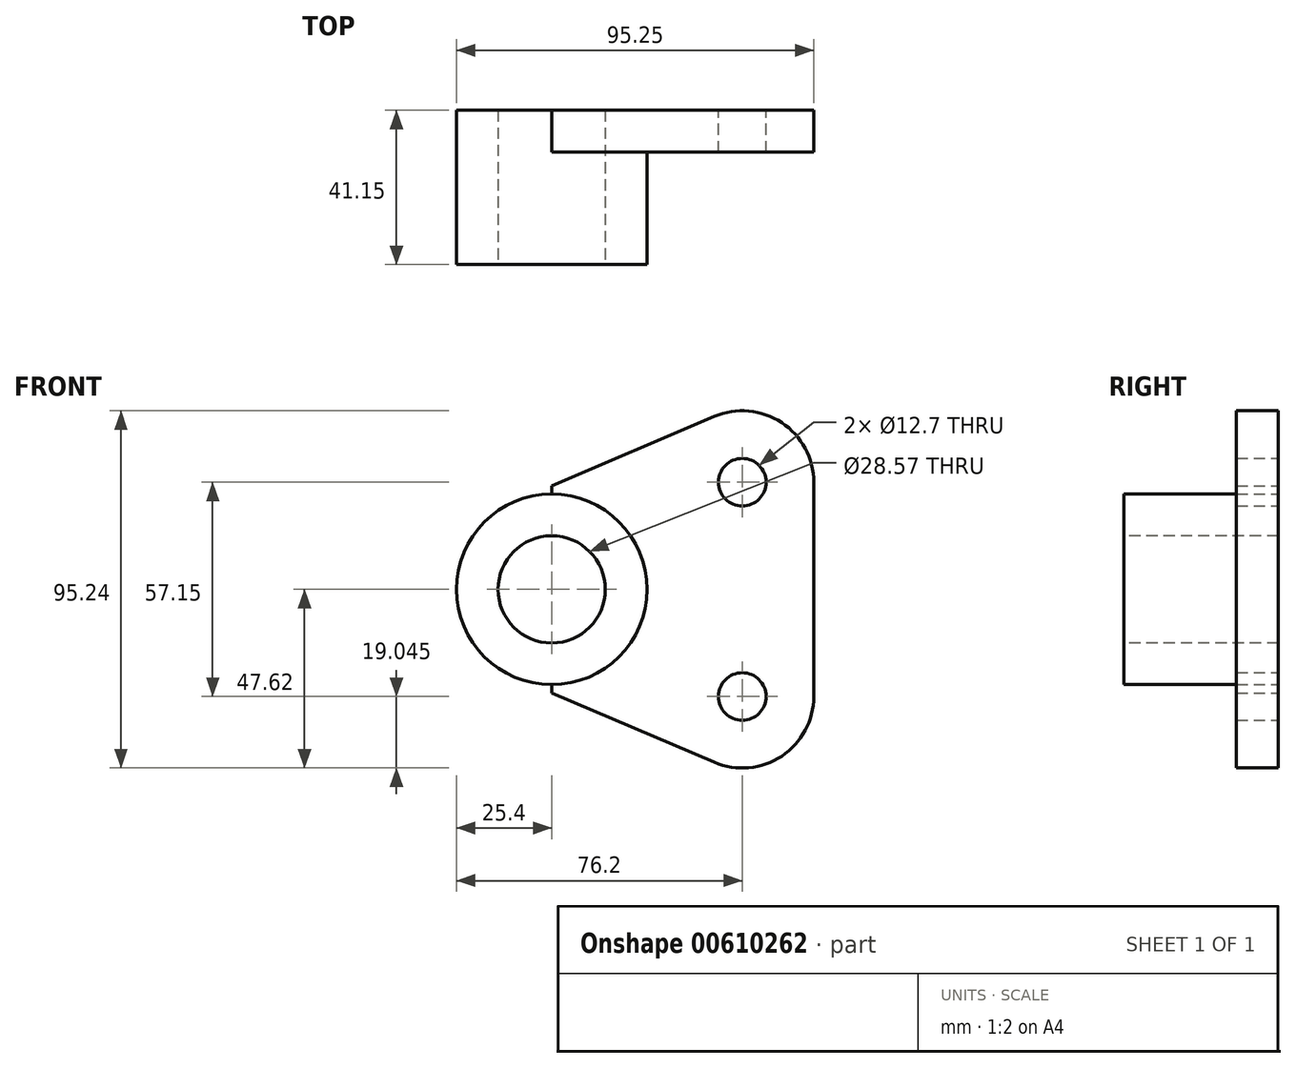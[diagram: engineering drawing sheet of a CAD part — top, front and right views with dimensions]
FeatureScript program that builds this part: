
annotation { "Feature Type Name" : "Feature", "Feature Type Description" : "" }
export const myFeature = defineFeature(function(context is Context, id is Id, definition is map)
    precondition{}
    {
        {
            var Q0;
            Q0=qCreatedBy(makeId("Front.planeOp"),FACE);
            var sketch = newSketch(context, id + "F0", { "sketchPlane" : qUnion([Q0])});
            skCircle(sketch, "E0", {"center": v(0, 0) * mm, "radius": 25.4 * mm});
            skSolve(sketch);
        }
        {
            var Q0;
            Q0 = qSketchRegion(id + "F0", true);
            var Q1;
            Q1=makeQuery(id+"F0.imprint","IMPRINT",FACE,{"disambiguationData":[TD([[makeQuery(id+"F0.imprint","IMPRINT",EDGE,{"derivedFrom":sQuery(id+"F0.wireOp",EDGE,"E0")}),1.0]])]});
            extrude(context, id + "F1", {"entities" : qUnion([Q0, Q1]), "depth" : 41.15 * mm, "offsetDistance" : 25.4 * mm});
        }
        {
            var Q0;
            Q0=makeQuery(id+"F1.opExtrude","CAP_FACE",FACE,{"disambiguationData":[OSD([sQuery(id+"F0.wireOp",EDGE,"E0")])],"isStart":false});
            var sketch = newSketch(context, id + "F2", { "sketchPlane" : qUnion([Q0])});
            skCircle(sketch, "E1", {"center": v(0, 0) * mm, "radius": 14.29 * mm});
            skSolve(sketch);
        }
        {
            var Q0;
            Q0=makeQuery(id+"F2.imprint","IMPRINT",FACE,{"disambiguationData":[TD([[makeQuery(id+"F2.imprint","IMPRINT",EDGE,{"derivedFrom":sQuery(id+"F2.wireOp",EDGE,"E1")}),1.0]])]});
            var Q1;
            Q1=sQuery(id+"F2.wireOp",EDGE,"E1");
            extrude(context, id + "F3", {"entities" : qUnion([Q0]), "operationType" : NewBodyOperationType.REMOVE, "surfaceEntities" : qUnion([Q1]), "oppositeDirection" : true, "depth" : 41.15 * mm, "offsetDistance" : 25.4 * mm});
        }
        {
            var Q0;
            Q0=qCreatedBy(makeId("Front.planeOp"),FACE);
            var sketch = newSketch(context, id + "F4", { "sketchPlane" : qUnion([Q0])});
            skArc(sketch, "E2", {"start": v(69.85, 28.58) * mm, "mid": v(61.3, 44.47) * mm, "end": v(43.33, 46.1) * mm});
            skArc(sketch, "E3", {"start": v(43.33, -46.1) * mm, "mid": v(61.3, -44.47) * mm, "end": v(69.85, -28.57) * mm});
            skCircle(sketch, "E4", {"center": v(50.8, -28.58) * mm, "radius": 6.35 * mm});
            skCircle(sketch, "E5", {"center": v(50.8, 28.58) * mm, "radius": 6.35 * mm});
            skLineSegment(sketch, "E6", {"start": v(69.85, 28.58) * mm, "end": v(69.85, -28.57) * mm});
            skLineSegment(sketch, "E7", {"start": v(43.33, -46.1) * mm, "end": v(0, -27.61) * mm});
            skLineSegment(sketch, "E8", {"start": v(43.33, 46.1) * mm, "end": v(0, 27.61) * mm});
            skLineSegment(sketch, "E9", {"start": v(0, 27.61) * mm, "end": v(0, -27.61) * mm});
            skPoint(sketch, "E10.end.orphan", {"position": v(50.8, 0) * mm});
            skSolve(sketch);
        }
        {
            var Q0;
            Q0=makeQuery(id+"F4.imprint","IMPRINT",FACE,{"disambiguationData":[TD([[makeQuery(id+"F4.imprint","IMPRINT",EDGE,{"derivedFrom":sQuery(id+"F4.wireOp",EDGE,"E2")}),1.0]])]});
            extrude(context, id + "F5", {"entities" : qUnion([Q0]), "operationType" : NewBodyOperationType.ADD, "depth" : 11.18 * mm, "offsetDistance" : 25.4 * mm});
        }
        {
            var Q0;
            {var subQ0=sQuery(id+"F4.wireOp",EDGE,"E9");Q0=makeQuery(id+"F5.boolean.opBoolean","SPLIT",FACE,{"disambiguationData":[TD([makeQuery(id+"F3.boolean.opBoolean","COPY",FACE,{"derivedFrom":makeQuery(id+"F3.opExtrude","SWEPT_FACE",FACE,{"disambiguationData":[OSD([sQuery(id+"F2.wireOp",EDGE,"E1")])]})})])],"derivedFrom":makeQuery(id+"F5.opExtrude","CAP_FACE",FACE,{"disambiguationData":[OSD([sQuery(id+"F4.wireOp",EDGE,"E2"),sQuery(id+"F4.wireOp",EDGE,"E3"),sQuery(id+"F4.wireOp",EDGE,"E4"),sQuery(id+"F4.wireOp",EDGE,"E5"),sQuery(id+"F4.wireOp",EDGE,"E6"),sQuery(id+"F4.wireOp",EDGE,"E7"),sQuery(id+"F4.wireOp",EDGE,"E8"),subQ0])],"isStart":false})});}
            extrude(context, id + "F6", {"entities" : qUnion([Q0]), "operationType" : NewBodyOperationType.REMOVE, "oppositeDirection" : true, "depth" : 11.18 * mm, "offsetDistance" : 25.4 * mm});
        }
    });
